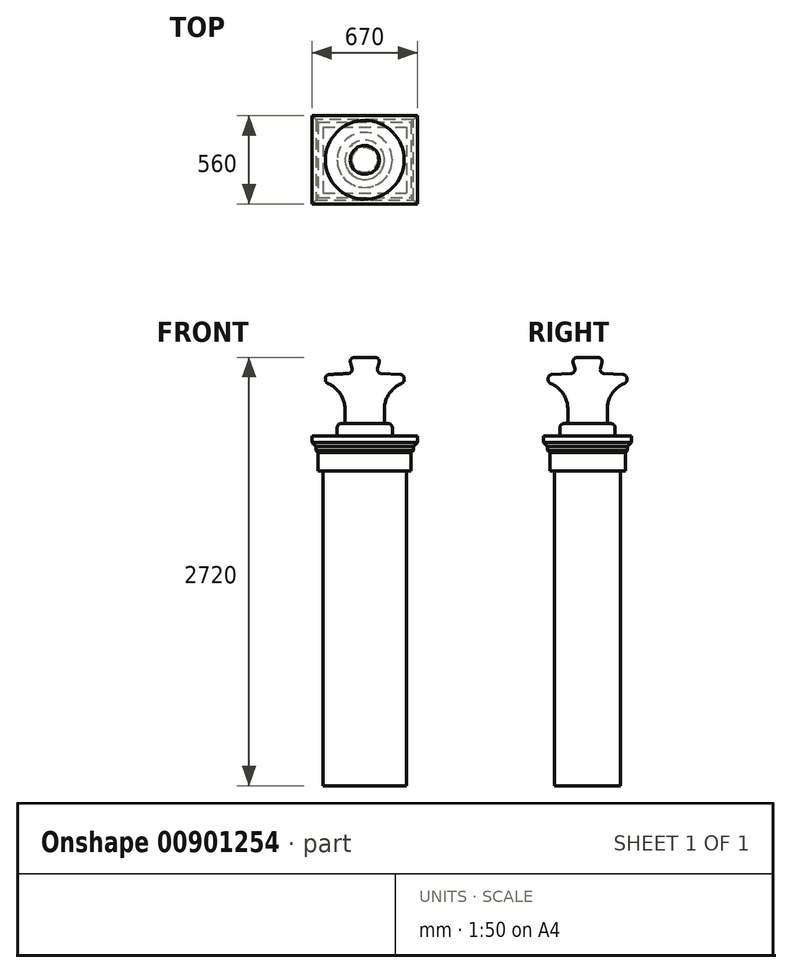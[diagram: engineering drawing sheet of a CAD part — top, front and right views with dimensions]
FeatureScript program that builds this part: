
annotation { "Feature Type Name" : "Feature", "Feature Type Description" : "" }
export const myFeature = defineFeature(function(context is Context, id is Id, definition is map)
    precondition{}
    {
        {
            var Q0;
            Q0=qCreatedBy(makeId("Top.planeOp"),FACE);
            var sketch = newSketch(context, id + "F0", { "sketchPlane" : qUnion([Q0])});
            skLineSegment(sketch, "E0.bottom", {"start": v(-265, 210) * mm, "end": v(265, 210) * mm});
            skLineSegment(sketch, "E0.top", {"start": v(-265, -210) * mm, "end": v(265, -210) * mm});
            skLineSegment(sketch, "E0.left", {"start": v(-265, 210) * mm, "end": v(-265, -210) * mm});
            skLineSegment(sketch, "E0.right", {"start": v(265, 210) * mm, "end": v(265, -210) * mm});
            skSolve(sketch);
        }
        {
            var Q0;
            Q0=qSketchRegion(id+"F0",true);
            extrude(context, id + "F1", {"entities" : qUnion([Q0]), "depth" : 2000 * mm, "offsetDistance" : 25.4 * mm});
        }
        {
            var Q0;
            Q0=makeQuery(id+"F1.opExtrude","CAP_FACE",FACE,{"disambiguationData":[OSD([sQuery(id+"F0.wireOp",EDGE,"E0.bottom"),sQuery(id+"F0.wireOp",EDGE,"E0.top"),sQuery(id+"F0.wireOp",EDGE,"E0.left"),sQuery(id+"F0.wireOp",EDGE,"E0.right")])],"isStart":false});
            var sketch = newSketch(context, id + "F2", { "sketchPlane" : qUnion([Q0])});
            skLineSegment(sketch, "E1.bottom", {"start": v(-295, 240) * mm, "end": v(295, 240) * mm});
            skLineSegment(sketch, "E1.top", {"start": v(-295, -240) * mm, "end": v(295, -240) * mm});
            skLineSegment(sketch, "E1.left", {"start": v(-295, 240) * mm, "end": v(-295, -240) * mm});
            skLineSegment(sketch, "E1.right", {"start": v(295, 240) * mm, "end": v(295, -240) * mm});
            skSolve(sketch);
        }
        {
            var Q0;
            Q0=qSketchRegion(id+"F2",true);
            extrude(context, id + "F3", {"entities" : qUnion([Q0]), "operationType" : NewBodyOperationType.ADD, "depth" : 100 * mm, "offsetDistance" : 25.4 * mm});
        }
        {
            var Q0;
            Q0=qCreatedBy(makeId("Right.planeOp"),FACE);
            var sketch = newSketch(context, id + "F4", { "sketchPlane" : qUnion([Q0])});
            skLineSegment(sketch, "E2.0", {"start": v(-240, 2100) * mm, "end": v(-240, 2000) * mm, "construction": true});
            skLineSegment(sketch, "E3.0", {"start": v(240, 2100) * mm, "end": v(-240, 2100) * mm, "construction": true});
            skLineSegment(sketch, "E4", {"start": v(-240, 2100) * mm, "end": v(-240, 2115) * mm});
            skLineSegment(sketch, "E5", {"start": v(-240, 2115) * mm, "end": v(-255, 2130) * mm});
            skLineSegment(sketch, "E6", {"start": v(-255, 2130) * mm, "end": v(-255, 2155) * mm});
            skLineSegment(sketch, "E7", {"start": v(-255, 2155) * mm, "end": v(-280, 2180) * mm});
            skLineSegment(sketch, "E8", {"start": v(-280, 2180) * mm, "end": v(-280, 2220) * mm});
            skLineSegment(sketch, "E9", {"start": v(-280, 2220) * mm, "end": v(-200, 2220) * mm});
            skLineSegment(sketch, "E10", {"start": v(-240, 2100) * mm, "end": v(-200, 2100) * mm});
            skLineSegment(sketch, "E11", {"start": v(-200, 2100) * mm, "end": v(-200, 2220) * mm});
            skPoint(sketch, "E12.orphan", {"position": v(-230, 2220) * mm});
            skSolve(sketch);
        }
        {
            var Q0;
            Q0=qSketchRegion(id+"F4",true);
            var Q1;
            Q1=makeQuery(id+"F3.opExtrude","CAP_EDGE",EDGE,{"disambiguationData":[OSD([sQuery(id+"F2.wireOp",EDGE,"E1.top")])],"isStart":false});
            var Q2;
            Q2=makeQuery(id+"F3.opExtrude","CAP_EDGE",EDGE,{"disambiguationData":[OSD([sQuery(id+"F2.wireOp",EDGE,"E1.right")])],"isStart":false});
            var Q3;
            Q3=makeQuery(id+"F3.opExtrude","CAP_EDGE",EDGE,{"disambiguationData":[OSD([sQuery(id+"F2.wireOp",EDGE,"E1.bottom")])],"isStart":false});
            var Q4;
            Q4=makeQuery(id+"F3.opExtrude","CAP_EDGE",EDGE,{"disambiguationData":[OSD([sQuery(id+"F2.wireOp",EDGE,"E1.left")])],"isStart":false});
            sweep(context, id + "F5", {"profiles" : qUnion([Q0]), "path" : qUnion([Q1, Q2, Q3, Q4])});
        }
        {
            var Q0;
            Q0=makeQuery(id+"F5.opSweep","SWEPT_FACE",FACE,{"disambiguationData":[OSD([sQuery(id+"F2.wireOp",EDGE,"E1.right"),sQuery(id+"F4.wireOp",EDGE,"E9")])]});
            var sketch = newSketch(context, id + "F6", { "sketchPlane" : qUnion([Q0])});
            skLineSegment(sketch, "E13.0", {"start": v(-255, 200) * mm, "end": v(-255, -200) * mm});
            skLineSegment(sketch, "E14.0", {"start": v(-255, -200) * mm, "end": v(255, -200) * mm});
            skLineSegment(sketch, "E15.0", {"start": v(255, -200) * mm, "end": v(255, 200) * mm});
            skLineSegment(sketch, "E16.0", {"start": v(255, 200) * mm, "end": v(-255, 200) * mm});
            skSolve(sketch);
        }
        {
            var Q0;
            Q0=qSketchRegion(id+"F6",true);
            var Q1;
            Q1=makeQuery(id+"F3.opExtrude","CAP_FACE",FACE,{"disambiguationData":[OSD([sQuery(id+"F2.wireOp",EDGE,"E1.bottom"),sQuery(id+"F2.wireOp",EDGE,"E1.top"),sQuery(id+"F2.wireOp",EDGE,"E1.left"),sQuery(id+"F2.wireOp",EDGE,"E1.right")])],"isStart":false});
            var Q2;
            Q2=makeQuery(id+"F5.opSweep","MID_CAP_VERTEX",VERTEX,{"disambiguationData":[OSD([sQuery(id+"F2.wireOp",EDGE,"E1.bottom"),sQuery(id+"F4.wireOp",EDGE,"E10"),sQuery(id+"F4.wireOp",EDGE,"E11")])],"capPos":2.0});
            extrude(context, id + "F7", {"entities" : qUnion([Q0]), "operationType" : NewBodyOperationType.ADD, "endBound" : BoundingType.UP_TO_SURFACE, "oppositeDirection" : true, "depth" : 25.4 * mm, "endBoundEntityFace" : qUnion([Q1]), "endBoundEntityVertex" : qUnion([Q2]), "offsetDistance" : 25.4 * mm});
        }
        {
            var Q0;
            Q0=qCreatedBy(makeId("Right.planeOp"),FACE);
            var sketch = newSketch(context, id + "F8", { "sketchPlane" : qUnion([Q0])});
            skLineSegment(sketch, "E17", {"start": v(0, 0) * mm, "end": v(0, 2720) * mm, "construction": true});
            skLineSegment(sketch, "E18.0", {"start": v(-280, 2220) * mm, "end": v(280, 2220) * mm, "construction": true});
            skLineSegment(sketch, "E19", {"start": v(0, 2720) * mm, "end": v(100, 2720) * mm});
            skLineSegment(sketch, "E20", {"start": v(100, 2720) * mm, "end": v(73.2, 2620) * mm});
            skLineSegment(sketch, "E21", {"start": v(73.2, 2620) * mm, "end": v(250, 2610.73) * mm});
            skLineSegment(sketch, "E22", {"start": v(250, 2610.73) * mm, "end": v(250, 2560.73) * mm});
            skLineSegment(sketch, "E23", {"start": v(250, 2560.73) * mm, "end": v(241.99, 2557.82) * mm});
            skLineSegment(sketch, "E24", {"start": v(0, 2220) * mm, "end": v(175, 2220) * mm});
            skLineSegment(sketch, "E25", {"start": v(175, 2220) * mm, "end": v(175, 2300) * mm});
            skLineSegment(sketch, "E26", {"start": v(175, 2300) * mm, "end": v(125, 2300) * mm});
            skLineSegment(sketch, "E27", {"start": v(125, 2300) * mm, "end": v(125, 2390.74) * mm});
            skLineSegment(sketch, "E28", {"start": v(73.2, 2620) * mm, "end": v(128.16, 2620) * mm, "construction": true});
            skLineSegment(sketch, "E29", {"start": v(0, 2720) * mm, "end": v(0, 2220) * mm});
            skArc(sketch, "E30", {"start": v(241.99, 2557.82) * mm, "mid": v(157.15, 2492.72) * mm, "end": v(125, 2390.74) * mm});
            skSolve(sketch);
        }
        {
            var Q0;
            Q0=qSketchRegion(id+"F8",true);
            var Q1;
            Q1=sQuery(id+"F8.wireOp",EDGE,"E17");
            revolve(context, id + "F9", {"operationType" : NewBodyOperationType.ADD, "surfaceOperationType" : NewSurfaceOperationType.NEW, "entities" : qUnion([Q0]), "axis" : qUnion([Q1]), "revolveType" : RevolveType.FULL});
        }
        {
            var Q0;
            Q0=makeQuery(id+"F9.opRevolve","SWEPT_EDGE",EDGE,{"disambiguationData":[OSD([sQuery(id+"F8.wireOp",EDGE,"E24"),sQuery(id+"F8.wireOp",EDGE,"E25")])]});
            var Q1;
            Q1=makeQuery(id+"F9.opRevolve","SWEPT_EDGE",EDGE,{"disambiguationData":[OSD([sQuery(id+"F8.wireOp",EDGE,"E25"),sQuery(id+"F8.wireOp",EDGE,"E26")])]});
            var Q2;
            Q2=makeQuery(id+"F9.opRevolve","SWEPT_EDGE",EDGE,{"disambiguationData":[OSD([sQuery(id+"F8.wireOp",EDGE,"E23"),sQuery(id+"F8.wireOp",EDGE,"g6WiTq2P-djQj-glQF-LKOc-a5rCoK2tAN3o")])]});
            var Q3;
            Q3=makeQuery(id+"F9.opRevolve","SWEPT_EDGE",EDGE,{"disambiguationData":[OSD([sQuery(id+"F8.wireOp",EDGE,"E20"),sQuery(id+"F8.wireOp",EDGE,"E21")])]});
            var Q4;
            Q4=makeQuery(id+"F9.opRevolve","SWEPT_EDGE",EDGE,{"disambiguationData":[OSD([sQuery(id+"F8.wireOp",EDGE,"E22"),sQuery(id+"F8.wireOp",EDGE,"E23")])]});
            var Q5;
            Q5=makeQuery(id+"F9.opRevolve","SWEPT_EDGE",EDGE,{"disambiguationData":[OSD([sQuery(id+"F8.wireOp",EDGE,"E21"),sQuery(id+"F8.wireOp",EDGE,"E22")])]});
            var Q6;
            Q6=makeQuery(id+"F9.opRevolve","SWEPT_EDGE",EDGE,{"disambiguationData":[OSD([sQuery(id+"F8.wireOp",EDGE,"E19"),sQuery(id+"F8.wireOp",EDGE,"E20")])]});
            fillet(context, id + "F10", {"entities" : qUnion([Q0, Q1, Q2, Q3, Q4, Q5, Q6]), "radius" : 25.4 * mm, "tangentPropagation" : true, "allowEdgeOverflow" : false});
        }
        {
            var Q0;
            Q0=makeQuery(id+"F9.opRevolve","SWEPT_EDGE",EDGE,{"disambiguationData":[OSD([sQuery(id+"F8.wireOp",EDGE,"E26"),sQuery(id+"F8.wireOp",EDGE,"E27")])]});
            fillet(context, id + "F11", {"entities" : qUnion([Q0]), "radius" : 19.05 * mm, "tangentPropagation" : true, "allowEdgeOverflow" : false});
        }
    });
